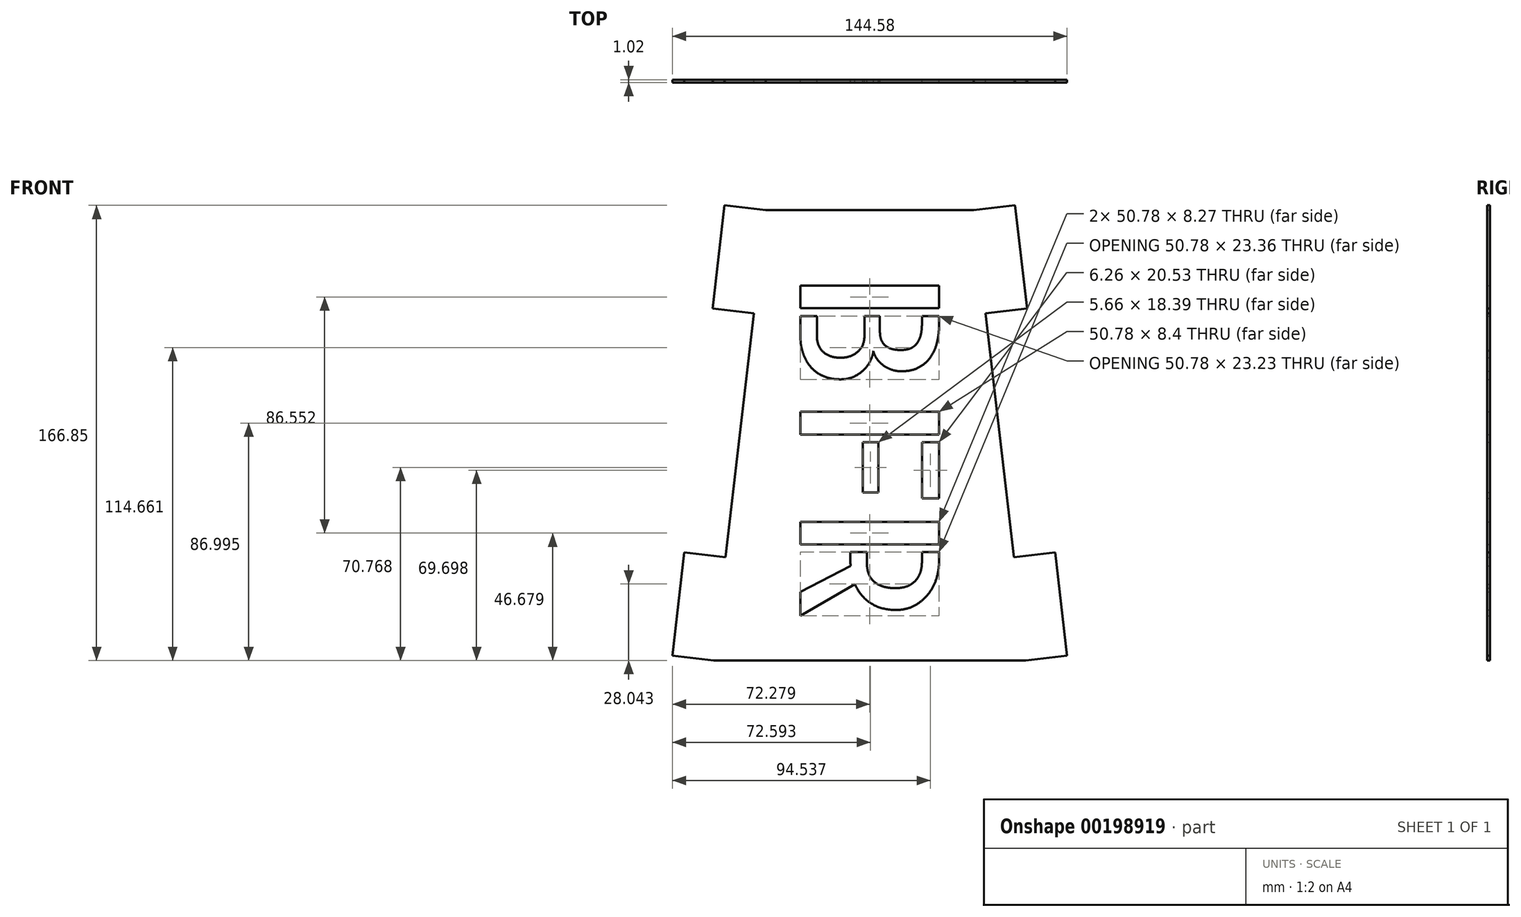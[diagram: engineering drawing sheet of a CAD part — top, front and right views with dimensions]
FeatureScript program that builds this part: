
annotation { "Feature Type Name" : "Feature", "Feature Type Description" : "" }
export const myFeature = defineFeature(function(context is Context, id is Id, definition is map)
    precondition{}
    {
        {
            var Q0;
            Q0=qCreatedBy(makeId("Front.planeOp"),FACE);
            var sketch = newSketch(context, id + "F0", { "sketchPlane" : qUnion([Q0])});
            skText(sketch, "E0", { "text": "BFR", "fontName": "AllertaStencil-Regular.ttf"});
            skLineSegment(sketch, "E1", {"start": v(0, 0) * mm, "end": v(114.3, 0) * mm});
            skLineSegment(sketch, "E2", {"start": v(109.93, 37.85) * mm, "end": v(99.62, 127.25) * mm});
            skLineSegment(sketch, "E3", {"start": v(95.25, 165.1) * mm, "end": v(19.05, 165.1) * mm});
            skLineSegment(sketch, "E4", {"start": v(14.68, 127.25) * mm, "end": v(4.37, 37.85) * mm});
            skLineSegment(sketch, "E5", {"start": v(19.05, 165.1) * mm, "end": v(3.91, 166.85) * mm});
            skLineSegment(sketch, "E6", {"start": v(3.91, 166.85) * mm, "end": v(-0.46, 129) * mm});
            skLineSegment(sketch, "E7", {"start": v(-0.46, 129) * mm, "end": v(14.68, 127.25) * mm});
            skLineSegment(sketch, "E8", {"start": v(114.3, 0) * mm, "end": v(129.44, 1.75) * mm});
            skLineSegment(sketch, "E9", {"start": v(129.44, 1.75) * mm, "end": v(125.07, 39.6) * mm});
            skLineSegment(sketch, "E10", {"start": v(125.07, 39.6) * mm, "end": v(109.93, 37.85) * mm});
            skLineSegment(sketch, "E11", {"start": v(0, 0) * mm, "end": v(-15.14, 1.75) * mm});
            skLineSegment(sketch, "E12", {"start": v(-15.14, 1.75) * mm, "end": v(-10.77, 39.6) * mm});
            skLineSegment(sketch, "E13", {"start": v(-10.77, 39.6) * mm, "end": v(4.37, 37.85) * mm});
            skLineSegment(sketch, "E14", {"start": v(95.25, 165.1) * mm, "end": v(110.39, 166.85) * mm});
            skLineSegment(sketch, "E15", {"start": v(110.39, 166.85) * mm, "end": v(114.76, 129) * mm});
            skLineSegment(sketch, "E16", {"start": v(114.76, 129) * mm, "end": v(99.62, 127.25) * mm});
            const initialGuessF0  = {"E0": [0.03175, 0.14398, 0, -1, 0.0508]};
            skSetInitialGuess(sketch, initialGuessF0);
            skSolve(sketch);
        }
        {
            var Q0;
            Q0 = qSketchRegion(id + "F0", true);
            extrude(context, id + "F1", {"entities" : qUnion([Q0]), "depth" : 1.02 * mm});
        }
    });
